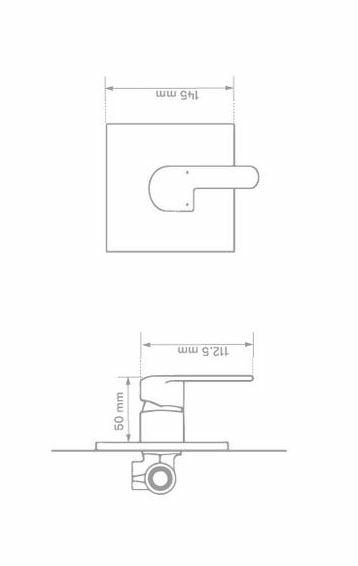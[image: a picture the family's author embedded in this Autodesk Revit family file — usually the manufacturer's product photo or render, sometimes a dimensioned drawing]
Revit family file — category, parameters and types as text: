
# Revit family: 01-3603-11-MEZCLADOR LAVAMANOS 8 FIRENZE PALA
name_source: partatom
category: Plumbing Fixtures
revit_build: Autodesk Revit 2018 (Build: 20170223_1515(x64)
units: mm (PartAtom-declared; Revit-internal decimal feet)

## family parameters
Cut with Voids When Loaded = No
Host = Face
OmniClass Number = 23.31.11.00
Part Type = Normal
Room Calculation Point = No
Round Connector Dimension = Use Diameter
Shared = No

## types (1)
- 01-3603-11
    Alto = 113 mm
    Ancho = 35 mm
    CW Connection = Yes
    Default Elevation = 0 mm  [stored 0 ft]
    Description = MEZCLADOR LAVAMANOS
    HW Connection = Yes
    Largo = 127 mm
    Link Ficha Tecnica = http://infotecnica.gricol.com
    Manufacturer = Gricol
    Model = 01-3603-11
    Plastico ABS Cromado = Plastico ABS Cromado
    Product Name = MEZCLADOR LAVAMANOS FIRENZE PALA
    Type Image = <None>
    URL = https://www.gricol.com
    Vent Connection = No
    Waste Connection = No

note: [stored X ft] marks values corroborated as IEEE doubles in the binary element streams (Revit-internal decimal feet)

## geometry (parser evidence)
native form markers: Blend x2, Sweep x14
no freeform markers — native parametric forms only
